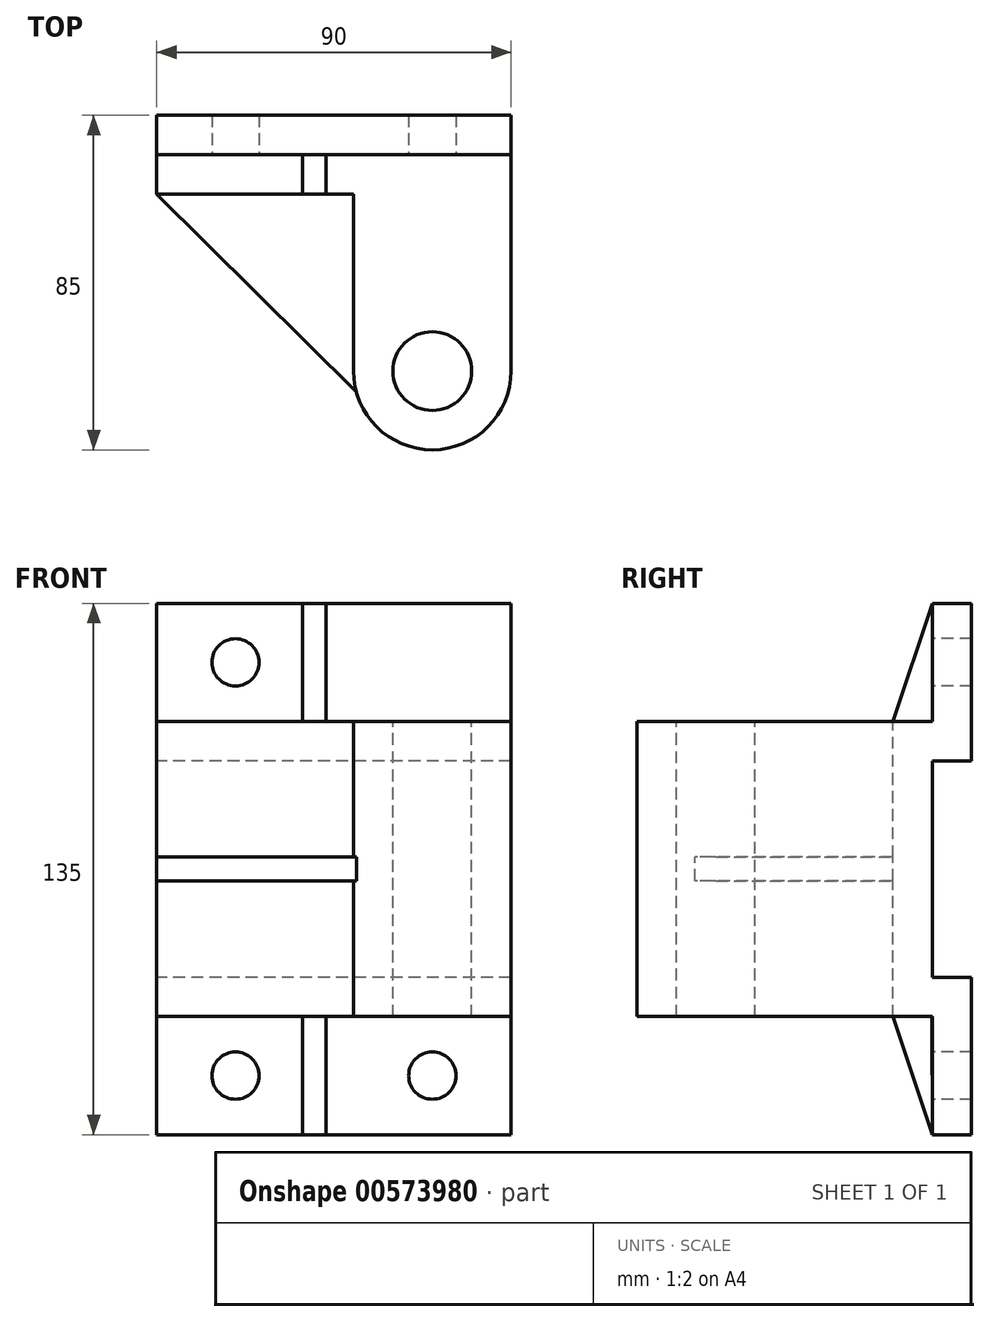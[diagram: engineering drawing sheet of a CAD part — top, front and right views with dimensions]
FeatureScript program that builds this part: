
annotation { "Feature Type Name" : "Feature", "Feature Type Description" : "" }
export const myFeature = defineFeature(function(context is Context, id is Id, definition is map)
    precondition{}
    {
        {
            var Q0;
            Q0=qCreatedBy(makeId("Front.planeOp"),FACE);
            var sketch = newSketch(context, id + "F0", { "sketchPlane" : qUnion([Q0])});
            skLineSegment(sketch, "E0.bottom", {"start": v(-45, 67.5) * mm, "end": v(45, 67.5) * mm});
            skLineSegment(sketch, "E0.top", {"start": v(-45, -67.5) * mm, "end": v(45, -67.5) * mm});
            skLineSegment(sketch, "E0.left", {"start": v(-45, 67.5) * mm, "end": v(-45, -67.5) * mm});
            skLineSegment(sketch, "E0.right", {"start": v(45, 67.5) * mm, "end": v(45, -67.5) * mm});
            skPoint(sketch, "E0.middle", {"position": v(0, 0) * mm});
            skSolve(sketch);
        }
        {
            var Q0;
            Q0 = qSketchRegion(id + "F0", true);
            extrude(context, id + "F1", {"entities" : qUnion([Q0]), "depth" : 20 * mm, "offsetDistance" : 25 * mm});
        }
        {
            var Q0;
            Q0=makeQuery(id+"F1.opExtrude","CAP_FACE",FACE,{"disambiguationData":[OSD([sQuery(id+"F0.wireOp",EDGE,"E0.bottom"),sQuery(id+"F0.wireOp",EDGE,"E0.top"),sQuery(id+"F0.wireOp",EDGE,"E0.left"),sQuery(id+"F0.wireOp",EDGE,"E0.right")])],"isStart":true});
            var sketch = newSketch(context, id + "F2", { "sketchPlane" : qUnion([Q0])});
            skLineSegment(sketch, "E1", {"start": v(-45, -27.5) * mm, "end": v(45, -27.5) * mm});
            skLineSegment(sketch, "E2", {"start": v(-45, 27.5) * mm, "end": v(45, 27.5) * mm});
            skSolve(sketch);
        }
        {
            var Q0;
            Q0 = qSketchRegion(id + "F2", true);
            var Q1;
            {var subQ0=sQuery(id+"F2.wireOp",EDGE,"E1");Q1=makeQuery(id+"F2.imprint","IMPRINT",FACE,{"disambiguationData":[TD([[makeQuery(id+"F2.imprint","IMPRINT",EDGE,{"derivedFrom":subQ0}),1.0]])]});}
            extrude(context, id + "F3", {"entities" : qUnion([Q0, Q1]), "operationType" : NewBodyOperationType.REMOVE, "oppositeDirection" : true, "depth" : 10 * mm, "offsetDistance" : 25 * mm});
        }
        {
            var Q0;
            Q0=makeQuery(id+"F1.opExtrude","CAP_FACE",FACE,{"disambiguationData":[OSD([sQuery(id+"F0.wireOp",EDGE,"E0.bottom"),sQuery(id+"F0.wireOp",EDGE,"E0.top"),sQuery(id+"F0.wireOp",EDGE,"E0.left"),sQuery(id+"F0.wireOp",EDGE,"E0.right")])],"isStart":false});
            var sketch = newSketch(context, id + "F4", { "sketchPlane" : qUnion([Q0])});
            skLineSegment(sketch, "E3", {"start": v(-45, 37.5) * mm, "end": v(45, 37.5) * mm});
            skLineSegment(sketch, "E4", {"start": v(-45, -37.5) * mm, "end": v(45, -37.5) * mm});
            skSolve(sketch);
        }
        {
            var Q0;
            Q0 = qSketchRegion(id + "F4", true);
            var Q1;
            {var subQ0=sQuery(id+"F4.wireOp",EDGE,"E3");Q1=makeQuery(id+"F4.imprint","IMPRINT",FACE,{"disambiguationData":[TD([[makeQuery(id+"F4.imprint","IMPRINT",EDGE,{"derivedFrom":subQ0}),1.0]])]});}
            var Q2;
            {var subQ0=sQuery(id+"F4.wireOp",EDGE,"E4");Q2=makeQuery(id+"F4.imprint","IMPRINT",FACE,{"disambiguationData":[TD([[makeQuery(id+"F4.imprint","IMPRINT",EDGE,{"derivedFrom":subQ0}),-1.0]])]});}
            extrude(context, id + "F5", {"entities" : qUnion([Q0, Q1, Q2]), "operationType" : NewBodyOperationType.REMOVE, "oppositeDirection" : true, "depth" : 10 * mm, "offsetDistance" : 25 * mm});
        }
        {
            var Q0;
            Q0=makeQuery(id+"F5.boolean.opBoolean","COPY",FACE,{"derivedFrom":makeQuery(id+"F5.opExtrude","SWEPT_FACE",FACE,{"disambiguationData":[OSD([sQuery(id+"F4.wireOp",EDGE,"E3")])]})});
            var sketch = newSketch(context, id + "F6", { "sketchPlane" : qUnion([Q0])});
            skLineSegment(sketch, "E5", {"start": v(-8, -20) * mm, "end": v(-2, -20) * mm});
            skSolve(sketch);
        }
        {
            var Q0;
            Q0=makeQuery(id+"F1.opExtrude","SWEPT_FACE",FACE,{"disambiguationData":[OSD([sQuery(id+"F0.wireOp",EDGE,"E0.left")])]});
            cPlane(context, id + "F7", {"entities" : qUnion([Q0]), "cplaneType" : CPlaneType.OFFSET, "offset" : 37 * mm, "oppositeDirection" : true, "width" : 150 * mm, "height" : 150 * mm});
        }
        {
            var Q0;
            Q0=qCreatedBy(id+"F7.planeOp",FACE);
            var sketch = newSketch(context, id + "F8", { "sketchPlane" : qUnion([Q0])});
            skLineSegment(sketch, "E6", {"start": v(20, 37.5) * mm, "end": v(10, 67.5) * mm});
            skLineSegment(sketch, "E7", {"start": v(10, 67.5) * mm, "end": v(10, 37.5) * mm});
            skLineSegment(sketch, "E8", {"start": v(10, 37.5) * mm, "end": v(20, 37.5) * mm});
            skSolve(sketch);
        }
        {
            var Q0;
            Q0 = qSketchRegion(id + "F8", true);
            extrude(context, id + "F9", {"entities" : qUnion([Q0]), "operationType" : NewBodyOperationType.ADD, "oppositeDirection" : true, "depth" : 6 * mm, "offsetDistance" : 25 * mm});
        }
        {
            var Q0;
            {var subQ0=sQuery(id+"F4.wireOp",EDGE,"E3");var subQ2=sQuery(id+"F0.wireOp",EDGE,"E0.left");var subQ3=sQuery(id+"F0.wireOp",EDGE,"E0.bottom");Q0=makeQuery(id+"F9.boolean.opBoolean","SPLIT",FACE,{"disambiguationData":[TD([makeQuery(id+"F1.opExtrude","SWEPT_FACE",FACE,{"disambiguationData":[OSD([subQ2])]})])],"derivedFrom":makeQuery(id+"F5.boolean.opBoolean","COPY",FACE,{"derivedFrom":makeQuery(id+"F5.opExtrude","CAP_FACE",FACE,{"disambiguationData":[OSD([subQ3,subQ2,sQuery(id+"F0.wireOp",EDGE,"E0.right"),subQ0])],"isStart":false})})});}
            var sketch = newSketch(context, id + "F10", { "sketchPlane" : qUnion([Q0])});
            skLineSegment(sketch, "E9", {"start": v(-45, 67.5) * mm, "end": v(-25, 67.5) * mm, "construction": true});
            skLineSegment(sketch, "E10", {"start": v(-25, 67.5) * mm, "end": v(-25, 52.5) * mm, "construction": true});
            skCircle(sketch, "E11", {"center": v(-25, 52.5) * mm, "radius": 6 * mm});
            skSolve(sketch);
        }
        {
            var Q0;
            {var subQ1=sQuery(id+"F4.wireOp",EDGE,"E3");var subQ2=sQuery(id+"F0.wireOp",EDGE,"E0.right");var subQ3=sQuery(id+"F0.wireOp",EDGE,"E0.bottom");Q0=makeQuery(id+"F9.boolean.opBoolean","SPLIT",FACE,{"disambiguationData":[TD([makeQuery(id+"F1.opExtrude","SWEPT_FACE",FACE,{"disambiguationData":[OSD([subQ2])]})])],"derivedFrom":makeQuery(id+"F5.boolean.opBoolean","COPY",FACE,{"derivedFrom":makeQuery(id+"F5.opExtrude","CAP_FACE",FACE,{"disambiguationData":[OSD([subQ3,sQuery(id+"F0.wireOp",EDGE,"E0.left"),subQ2,subQ1])],"isStart":false})})});}
            var sketch = newSketch(context, id + "F11", { "sketchPlane" : qUnion([Q0])});
            skSolve(sketch);
        }
        {
            var Q0;
            {var subQ4=sQuery(id+"F8.wireOp",EDGE,"E7");Q0=makeQuery(id+"F11.imprint","IMPRINT",FACE,{"disambiguationData":[TD([[makeQuery(id+"F11.imprint","IMPRINT",EDGE,{"derivedFrom":makeQuery(id+"F9.opExtrude","CAP_EDGE",EDGE,{"disambiguationData":[OSD([subQ4])],"isStart":false})}),1.0]])]});}
            var sketch = newSketch(context, id + "F12", { "sketchPlane" : qUnion([Q0])});
            skLineSegment(sketch, "E12", {"start": v(-25, 52.5) * mm, "end": v(25, 52.5) * mm, "construction": true});
            skCircle(sketch, "E13", {"center": v(25, 52.5) * mm, "radius": 6 * mm});
            skSolve(sketch);
        }
        {
            var Q0;
            Q0=makeQuery(id+"F10.imprint","IMPRINT",FACE,{"disambiguationData":[TD([[makeQuery(id+"F10.imprint","IMPRINT",EDGE,{"derivedFrom":sQuery(id+"F10.wireOp",EDGE,"E11")}),1.0]])]});
            var Q1;
            Q1=makeQuery(id+"F12.imprint","IMPRINT",FACE,{"disambiguationData":[TD([[makeQuery(id+"F12.imprint","IMPRINT",EDGE,{"derivedFrom":sQuery(id+"F12.wireOp",EDGE,"E13")}),1.0]])]});
            extrude(context, id + "F13", {"entities" : qUnion([Q0, Q1]), "operationType" : NewBodyOperationType.REMOVE, "endBound" : BoundingType.THROUGH_ALL, "oppositeDirection" : true, "depth" : 25 * mm, "offsetDistance" : 25 * mm});
        }
        {
            var Q0;
            Q0=makeQuery(id+"F1.opExtrude","SWEPT_FACE",FACE,{"disambiguationData":[OSD([sQuery(id+"F0.wireOp",EDGE,"E0.left")])]});
            cPlane(context, id + "F14", {"entities" : qUnion([Q0]), "cplaneType" : CPlaneType.OFFSET, "offset" : 37 * mm, "oppositeDirection" : true, "width" : 150 * mm, "height" : 150 * mm});
        }
        {
            var Q0;
            Q0=qCreatedBy(id+"F14.planeOp",FACE);
            var sketch = newSketch(context, id + "F15", { "sketchPlane" : qUnion([Q0])});
            skLineSegment(sketch, "E14", {"start": v(10, -67.5) * mm, "end": v(20, -37.5) * mm});
            skLineSegment(sketch, "E15", {"start": v(20, -37.5) * mm, "end": v(10.04, -37.5) * mm});
            skLineSegment(sketch, "E16", {"start": v(10.04, -37.5) * mm, "end": v(10, -67.5) * mm});
            skSolve(sketch);
        }
        {
            var Q0;
            Q0 = qSketchRegion(id + "F15", true);
            extrude(context, id + "F16", {"entities" : qUnion([Q0]), "operationType" : NewBodyOperationType.ADD, "oppositeDirection" : true, "depth" : 6 * mm, "offsetDistance" : 25 * mm});
        }
        {
            var Q0;
            Q0=makeQuery(id+"F5.boolean.opBoolean","COPY",FACE,{"derivedFrom":makeQuery(id+"F5.opExtrude","CAP_FACE",FACE,{"disambiguationData":[OSD([sQuery(id+"F0.wireOp",EDGE,"E0.top"),sQuery(id+"F0.wireOp",EDGE,"E0.left"),sQuery(id+"F0.wireOp",EDGE,"E0.right"),sQuery(id+"F4.wireOp",EDGE,"E4")])],"isStart":false})});
            var sketch = newSketch(context, id + "F17", { "sketchPlane" : qUnion([Q0])});
            skLineSegment(sketch, "E17", {"start": v(-45, -67.5) * mm, "end": v(-25, -67.5) * mm, "construction": true});
            skLineSegment(sketch, "E18", {"start": v(-25, -67.5) * mm, "end": v(-25, -52.5) * mm, "construction": true});
            skCircle(sketch, "E19", {"center": v(-25, -52.5) * mm, "radius": 6 * mm});
            skLineSegment(sketch, "E20", {"start": v(-25, -52.5) * mm, "end": v(25, -52.5) * mm, "construction": true});
            skCircle(sketch, "E21", {"center": v(25, -52.5) * mm, "radius": 6 * mm});
            skSolve(sketch);
        }
        {
            var Q0;
            Q0 = qSketchRegion(id + "F17", true);
            extrude(context, id + "F18", {"entities" : qUnion([Q0]), "operationType" : NewBodyOperationType.REMOVE, "endBound" : BoundingType.THROUGH_ALL, "oppositeDirection" : true, "depth" : 25 * mm, "offsetDistance" : 25 * mm});
        }
        {
            var Q0;
            Q0=makeQuery(id+"F1.opExtrude","SWEPT_FACE",FACE,{"disambiguationData":[OSD([sQuery(id+"F0.wireOp",EDGE,"E0.bottom")])]});
            cPlane(context, id + "F19", {"entities" : qUnion([Q0]), "cplaneType" : CPlaneType.OFFSET, "offset" : 30 * mm, "oppositeDirection" : true, "width" : 150 * mm, "height" : 150 * mm});
        }
        {
            var Q0;
            Q0=qCreatedBy(id+"F19.planeOp",FACE);
            var sketch = newSketch(context, id + "F20", { "sketchPlane" : qUnion([Q0])});
            skLineSegment(sketch, "E22", {"start": v(5, -20) * mm, "end": v(45, -20) * mm});
            skLineSegment(sketch, "E23", {"start": v(25, -20) * mm, "end": v(25, -65) * mm, "construction": true});
            skArc(sketch, "E24", {"start": v(5, -65) * mm, "mid": v(25, -85) * mm, "end": v(45, -65) * mm});
            skLineSegment(sketch, "E25", {"start": v(45, -20) * mm, "end": v(45, -65) * mm});
            skLineSegment(sketch, "E26.MirrorCS", {"start": v(5, -20) * mm, "end": v(5, -65) * mm});
            skCircle(sketch, "E27", {"center": v(25, -65) * mm, "radius": 10 * mm});
            skSolve(sketch);
        }
        {
            var Q0;
            Q0=makeQuery(id+"F20.imprint","IMPRINT",FACE,{"disambiguationData":[TD([[makeQuery(id+"F20.imprint","IMPRINT",EDGE,{"derivedFrom":sQuery(id+"F20.wireOp",EDGE,"E22")}),-1.0]])]});
            extrude(context, id + "F21", {"entities" : qUnion([Q0]), "operationType" : NewBodyOperationType.ADD, "oppositeDirection" : true, "depth" : 75 * mm, "offsetDistance" : 25 * mm});
        }
        {
            var Q0;
            {var subQ3=sQuery(id+"F6.wireOp",EDGE,"E5");Q0=makeQuery(id+"F6.imprint","IMPRINT",FACE,{"disambiguationData":[TD([[makeQuery(id+"F6.imprint","IMPRINT",EDGE,{"derivedFrom":subQ3}),1.0]])]});}
            cPlane(context, id + "F22", {"entities" : qUnion([Q0]), "cplaneType" : CPlaneType.OFFSET, "offset" : 34.5 * mm, "oppositeDirection" : true, "width" : 150 * mm, "height" : 150 * mm});
        }
        {
            var Q0;
            Q0=qCreatedBy(id+"F22.planeOp",FACE);
            var sketch = newSketch(context, id + "F23", { "sketchPlane" : qUnion([Q0])});
            skLineSegment(sketch, "E28", {"start": v(-45, -20) * mm, "end": v(6.63, -71.23) * mm});
            skLineSegment(sketch, "E29", {"start": v(6.63, -71.23) * mm, "end": v(5, -20) * mm});
            skLineSegment(sketch, "E30", {"start": v(5, -20) * mm, "end": v(-45, -20) * mm});
            skSolve(sketch);
        }
        {
            var Q0;
            Q0 = qSketchRegion(id + "F23", true);
            extrude(context, id + "F24", {"entities" : qUnion([Q0]), "operationType" : NewBodyOperationType.ADD, "oppositeDirection" : true, "depth" : 6 * mm, "offsetDistance" : 25 * mm});
        }
    });
